# Revit family: 5150229300676
name_source: partatom
category: Plumbing Fixtures
units: mm (PartAtom-declared; Revit-internal decimal feet)

## family parameters
Always vertical = Yes
Cut with Voids When Loaded = No
OmniClass Number = 23.45.55.00
OmniClass Title = Sanitary Faucets, Wastes
Part Type = Normal
Room Calculation Point = No
Round Connector Dimension = Use Diameter
Shared = No
Work Plane-Based = No

## types (1)
- 5150229300676 Washbasin faucet
    2D/3D/BIM Files URL = http://static.hansa.com
    3D View = https://static.hansa.com
    Advanced Features = Inner body made of DZR brass;Rapid installation system
    Aerator = PCA® - constant flow rate regardless of pressure variations
    Approval ABP = P-IX 29493/IA
    Approval KIWA = K6116/08
    AssetType = Fixed
    BIMObjectName = 5150229300676
    Backflow Prevention EN1717 = AA
    BodyMaterial = Brass
    Brand = HANSA
    CO2 Emissions (A1-A3) = 9.09
    CO2 Emissions (A4) = 0.25
    CO2 Emissions (B7) = 1483.2
    CO2 Emissions (C2) = 0.02
    CO2 Emissions (C3) = 0.02
    CO2 Emissions (C4) = 0.07
    CO2 Emissions (D) = -6.47
    Catalog Drawing URL = http://static.hansa.com
    Category = Washbasin
    CloseOffRating = 0
    Color = Chrome
    Connection = Flexible inlet pipes
    Connection Size = G3/8
    Default Elevation = 0 mm  [stored 0 ft]
    Description = Washbasin faucet with fixed spout and aerator
    Dimension Drawing URL = http://static.hansa.com
    DurationUnit = Year
    EAN Number = 4057304004001
    EN Standard = EN 817
    ETIM Class Number = EC011328 Washbasin mixing tap
    Eco Flow At 300kPa = 0.1 L/s
    Extensions = Pop-up waste with draw-rod
    FDV Document URL = http://www.hansa.com
    FaucetMainMaterial = Brass
    Features = Single-lever;
    Finish = Polished
    Flow Drawing URL = http://static.hansa.com
    Flow Rate At 300kPa = 0.2 L/s
    Flow Rate At 300kPa With Flow Controller = 0.1 L/s
    FlowCoefficient = 0
    Group = Washbasin faucet
    IfcExportAs = IfcValveType
    IfcExportType = FAUCET
    InletConnectionSize = 10 mm  [stored 0.0328084 ft]
    Installation Type = Deck mounted
    Installation and Maintenance Guide URL = http://static.hansa.com
    Interactive AR View URL = https://static.hansa.com
    Lever Handle = Hot/Cold symbols;Single operating lever/handle
    Manufacturer = HANSA
    ManufacturerName = HANSA
    ManufacturerURL = http://www.hansa.com
    Market = International;Germany;Belgium;Netherlands;France;Czech Republic;Slovakia;Italy;Spain
    Material = Brass
    Max. Hot Water Supply = 70 °C
    Mechanical Parts = ø 35 mm ceramic cartridge for flow and temperature control
    Mobile Product Information URL = http://mpi.hansa.com
    Model = 5150229300676 Washbasin faucet
    ModelReference = 5150229300676
    Mounting Holes = 1 hole
    NBSDescription = Water supply fittings for wash basins and troughs
    NBSReference = 45-35-70/371
    Name = 5150229300676 Washbasin faucet
    Name_en = 5150229300676 Washbasin faucet
    Noise Class = I (ISO3822)
    NominalDepth = 160 mm
    NominalHeight = 157 mm  [stored 0.515092 ft]
    NominalWidth = 49 mm  [stored 0.160761 ft]
    Product Code = 5150229300676
    Product Family = HANSAPOLO Eco
    Product Image URL = http://static.hansa.com
    Product URL = http://static.hansa.com
    ProductInformation = Washbasin faucet with fixed spout and aerator
    Sales Package dimensions (LxWxH) = 380 x 180 x 74
    Shape = Sculptured
    Size = 48.5x160x160 mm
    Spout Projection = 110 mm
    Spout Type = Fixed spout
    Surface treatment = Chrome
    Technical DataSheet URL = http://www.hansa.com
    Temperature = Temperature limiter;;Temperature limiter (retrofittable)
    Temperature Adjustments = Limitation option for maximum temperature and flow-rate ;Energy saving variation - cold water in the middle position;Adjustable hot water stop (included, retrofittable)
    UNSPSC Class Number = 30181700 Faucets or taps
    URL ABP = http://static.hansa.com
    URL Declaration Of Performance (DOP) = http://static.hansa.com
    URL Declaration of Asbestos = http://static.hansa.com
    URL Declaration of Conformity = http://static.hansa.com
    URL Declaration of SCIP = http://static.hansa.com
    URL EU Packaging Declaration = http://static.hansa.com
    URL EcoLabel Declaration = http://static.hansa.com
    URL Environmental Product Declaration EPD = http://www.hansa.com faucet.pdf
    URL KIWA = http://static.hansa.com
    URL Materials Declaration = http://www.hansa.com
    URL REACH = http://static.hansa.com
    URL UWL = http://static.hansa.com
    Uniclass2 = Pr_40_30_96_96
    Uniclass2015Description = Washbasin manual water supply sets
    Uniclass2015Reference = Pr_40_20_87_96
    Version = 1
    VersionDate = 01/06/2023
    Warranty Information URL = http://warranty.hansa.com
    WarrantyDescription = http://warranty.hansa.com
    WarrantyDurationUnit = Year
    Working Pressure = 50 - 1000 kPa

note: [stored X ft] marks values corroborated as IEEE doubles in the binary element streams (Revit-internal decimal feet)

## geometry (parser evidence)
native form markers: Sweep x6
no freeform markers — native parametric forms only
